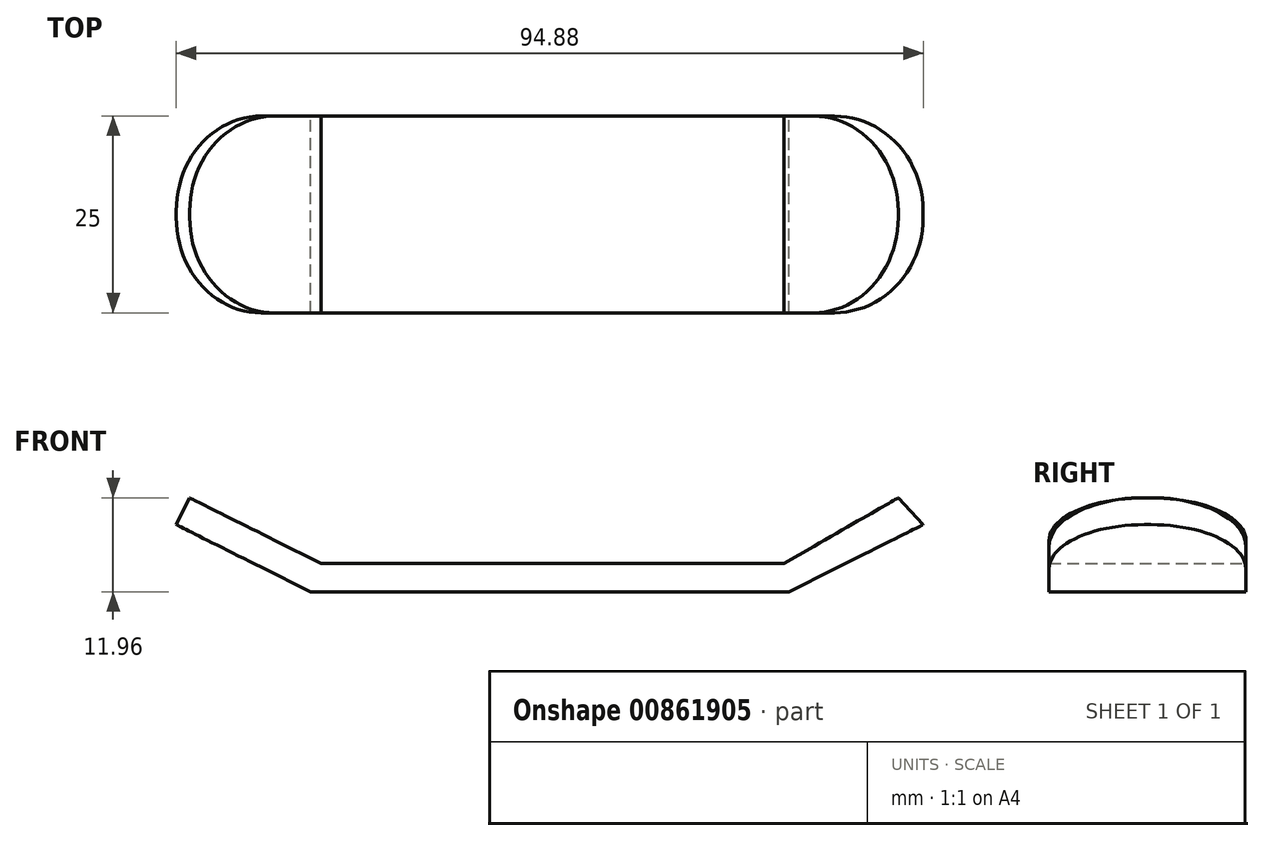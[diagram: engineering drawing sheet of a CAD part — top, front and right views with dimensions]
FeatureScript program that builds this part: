
annotation { "Feature Type Name" : "Feature", "Feature Type Description" : "" }
export const myFeature = defineFeature(function(context is Context, id is Id, definition is map)
    precondition{}
    {
        {
            var Q0;
            Q0=qCreatedBy(makeId("Front.planeOp"),FACE);
            var sketch = newSketch(context, id + "F0", { "sketchPlane" : qUnion([Q0])});
            skLineSegment(sketch, "E0", {"start": v(-38.74, -19.77) * mm, "end": v(21.98, -19.77) * mm});
            skLineSegment(sketch, "E1", {"start": v(21.98, -19.77) * mm, "end": v(39.06, -11.23) * mm});
            skLineSegment(sketch, "E2", {"start": v(-38.74, -19.77) * mm, "end": v(-55.82, -11.23) * mm});
            skLineSegment(sketch, "E3", {"start": v(-55.82, -11.23) * mm, "end": v(-54.11, -7.81) * mm});
            skLineSegment(sketch, "E4", {"start": v(-54.11, -7.81) * mm, "end": v(-37.41, -16.16) * mm});
            skLineSegment(sketch, "E5", {"start": v(-37.41, -16.16) * mm, "end": v(21.35, -16.16) * mm});
            skLineSegment(sketch, "E6", {"start": v(21.35, -16.16) * mm, "end": v(35.9, -7.81) * mm});
            skLineSegment(sketch, "E7", {"start": v(35.9, -7.81) * mm, "end": v(39.06, -11.23) * mm});
            skSolve(sketch);
        }
        {
            var Q0;
            Q0 = qSketchRegion(id + "F0", true);
            extrude(context, id + "F1", {"entities" : qUnion([Q0]), "depth" : 25 * mm, "offsetDistance" : 25 * mm});
        }
        {
            var Q0;
            Q0=makeQuery(id+"F1.opExtrude","CAP_EDGE",EDGE,{"disambiguationData":[OSD([sQuery(id+"F0.wireOp",EDGE,"E3")])],"isStart":false});
            var Q1;
            Q1=makeQuery(id+"F1.opExtrude","CAP_EDGE",EDGE,{"disambiguationData":[OSD([sQuery(id+"F0.wireOp",EDGE,"E7")])],"isStart":false});
            var Q2;
            Q2=makeQuery(id+"F1.opExtrude","CAP_EDGE",EDGE,{"disambiguationData":[OSD([sQuery(id+"F0.wireOp",EDGE,"E3")])],"isStart":true});
            var Q3;
            Q3=makeQuery(id+"F1.opExtrude","CAP_EDGE",EDGE,{"disambiguationData":[OSD([sQuery(id+"F0.wireOp",EDGE,"E7")])],"isStart":true});
            fillet(context, id + "F2", {"entities" : qUnion([Q0, Q1, Q2, Q3]), "radius" : 12.07 * mm, "tangentPropagation" : true, "allowEdgeOverflow" : false});
        }
    });
